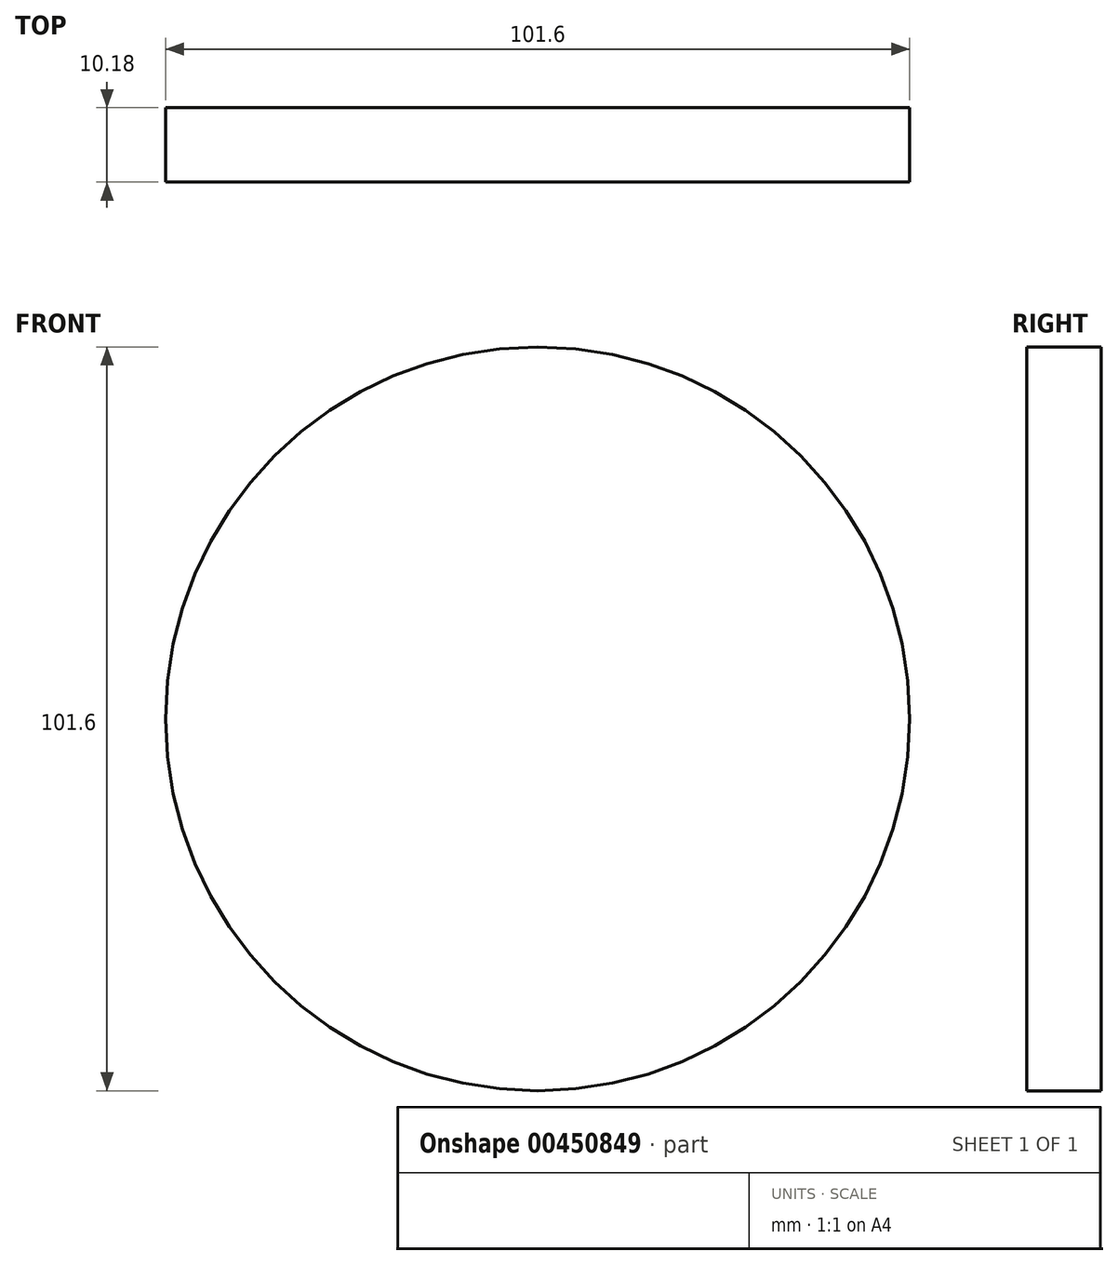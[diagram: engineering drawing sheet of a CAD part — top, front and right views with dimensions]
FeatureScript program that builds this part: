
annotation { "Feature Type Name" : "Feature", "Feature Type Description" : "" }
export const myFeature = defineFeature(function(context is Context, id is Id, definition is map)
    precondition{}
    {
        {
            assignVariable(context, id + "F0", {"name" : "marbleDiam", "anyValue" : 10.16 * mm});
        }
        {
            var Q0;
            Q0=qCreatedBy(makeId("Front.planeOp"),FACE);
            var sketch = newSketch(context, id + "F1", { "sketchPlane" : qUnion([Q0])});
            skCircle(sketch, "E0", {"center": v(0, 0) * mm, "radius": 50.8 * mm});
            skSolve(sketch);
        }
        {
            var Q0;
            Q0=makeQuery(id+"F1.imprint","IMPRINT",FACE,{"disambiguationData":[TD([[makeQuery(id+"F1.imprint","IMPRINT",EDGE,{"derivedFrom":sQuery(id+"F1.wireOp",EDGE,"E0")}),1.0]])]});
            extrude(context, id + "F2", {"entities" : qUnion([Q0]), "depth" : (7 / 406.4 * mm + getVariable(context, 'marbleDiam'))});
        }
    });
